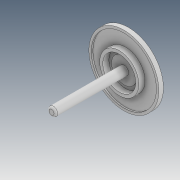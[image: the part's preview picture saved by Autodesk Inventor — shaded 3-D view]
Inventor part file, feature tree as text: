
AUTODESK INVENTOR PART (.ipt)
format: ipt  version: 2020 (Build 240168000, 168)  size: 128,000 bytes
history: native  units: mm
features: extrude x5, sketch x5, fillet x1, projected_geometry x1
ambient origin geometry x8: Origin, YZ Plane, XZ Plane, XY Plane, X Axis, Y Axis, Z Axis, Center Point
bodies: Solid1 (feature_tree)
feature tree (12):
  extrude  "Extrusion1"  Depth=1.0mm TaperAngle=0.0deg
  extrude  "Extrusion2"  Depth=0.5mm TaperAngle=0.0deg
  extrude  "Extrusion3"  Depth=10.75mm
  extrude  "Extrusion4"  Depth=24.1mm
  fillet  "Fillet1"  Radius=24.1mm
  extrude  "Extrusion5"  Depth=0.4mm
  sketch  "Sketch1"  dims[d0=22.8mm d1=1.0mm d2=0.0mm]
  sketch  "Sketch2"  dims[d3=0.8mm d4=0.5mm d5=0.0mm]
  projected_geometry  "Projected Loop1"
  sketch  "Sketch3"  dims[d6=12.75mm d7=10.75mm]
  sketch  "Sketch4"  dims[d8=2.0mm d9=0.0mm d10=2.85mm d11=24.1mm d12=0.0mm]
  sketch  "Sketch5"  dims[d13=0.6mm d14=8.25mm d15=0.4mm d16=0.0mm]
